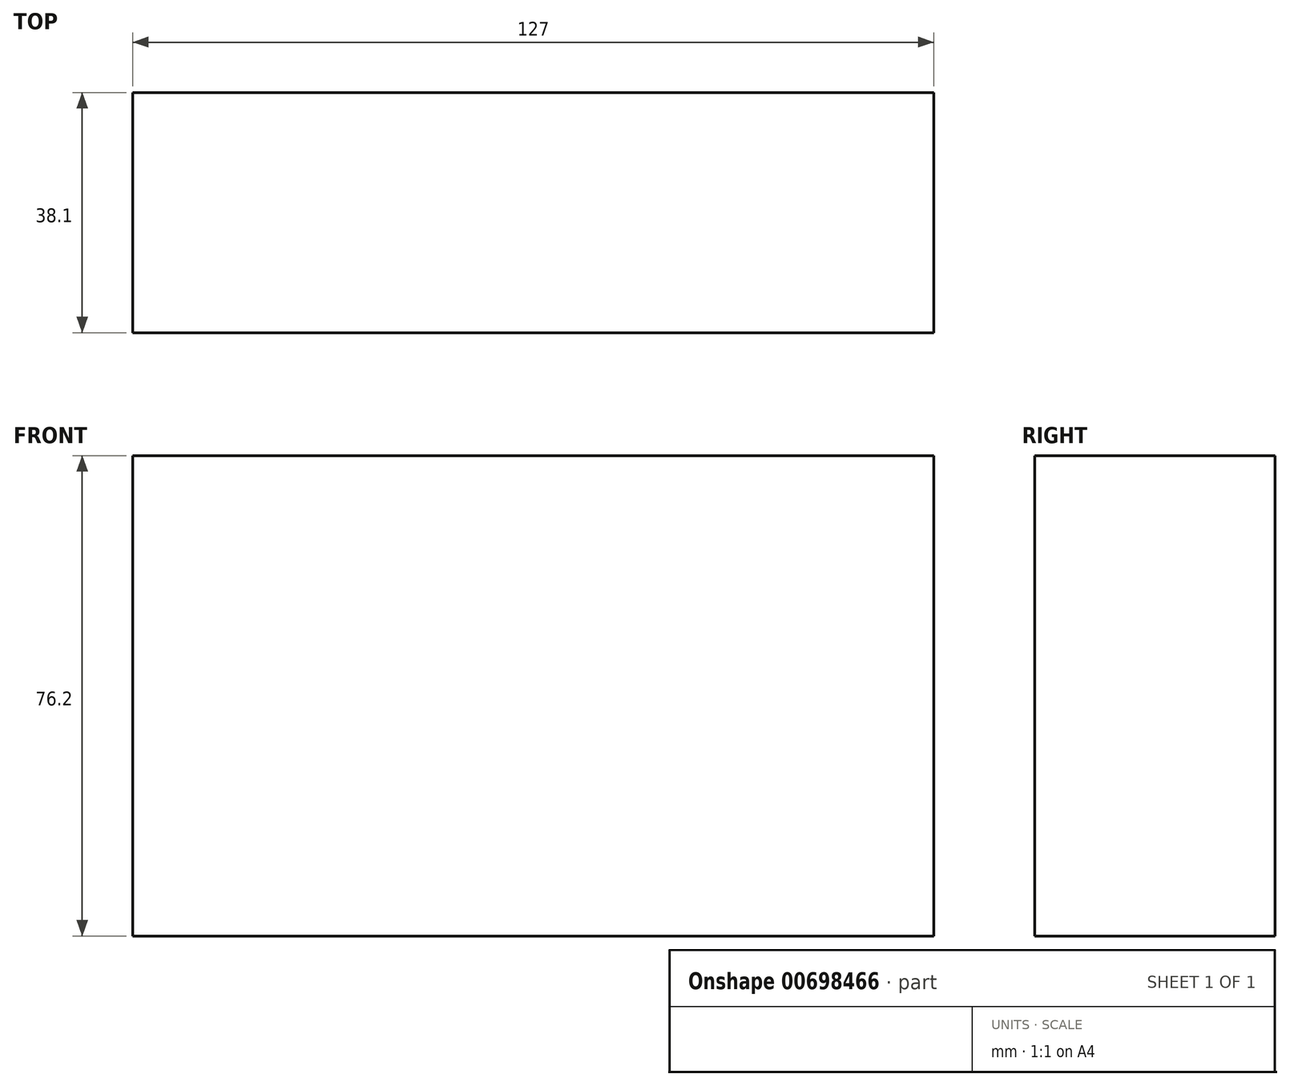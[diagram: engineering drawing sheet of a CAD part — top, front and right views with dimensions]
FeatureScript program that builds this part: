
annotation { "Feature Type Name" : "Feature", "Feature Type Description" : "" }
export const myFeature = defineFeature(function(context is Context, id is Id, definition is map)
    precondition{}
    {
        {
            var Q0;
            Q0=qCreatedBy(makeId("Front.planeOp"),FACE);
            var sketch = newSketch(context, id + "F0", { "sketchPlane" : qUnion([Q0])});
            skLineSegment(sketch, "E0.bottom", {"start": v(-88.9, 38.1) * mm, "end": v(38.1, 38.1) * mm});
            skLineSegment(sketch, "E0.top", {"start": v(-88.9, -38.1) * mm, "end": v(38.1, -38.1) * mm});
            skLineSegment(sketch, "E0.left", {"start": v(-88.9, 38.1) * mm, "end": v(-88.9, -38.1) * mm});
            skLineSegment(sketch, "E0.right", {"start": v(38.1, 38.1) * mm, "end": v(38.1, -38.1) * mm});
            skSolve(sketch);
        }
        {
            var Q0;
            Q0 = qSketchRegion(id + "F0", true);
            extrude(context, id + "F1", {"entities" : qUnion([Q0]), "depth" : 38.1 * mm, "offsetDistance" : 25.4 * mm});
        }
    });
